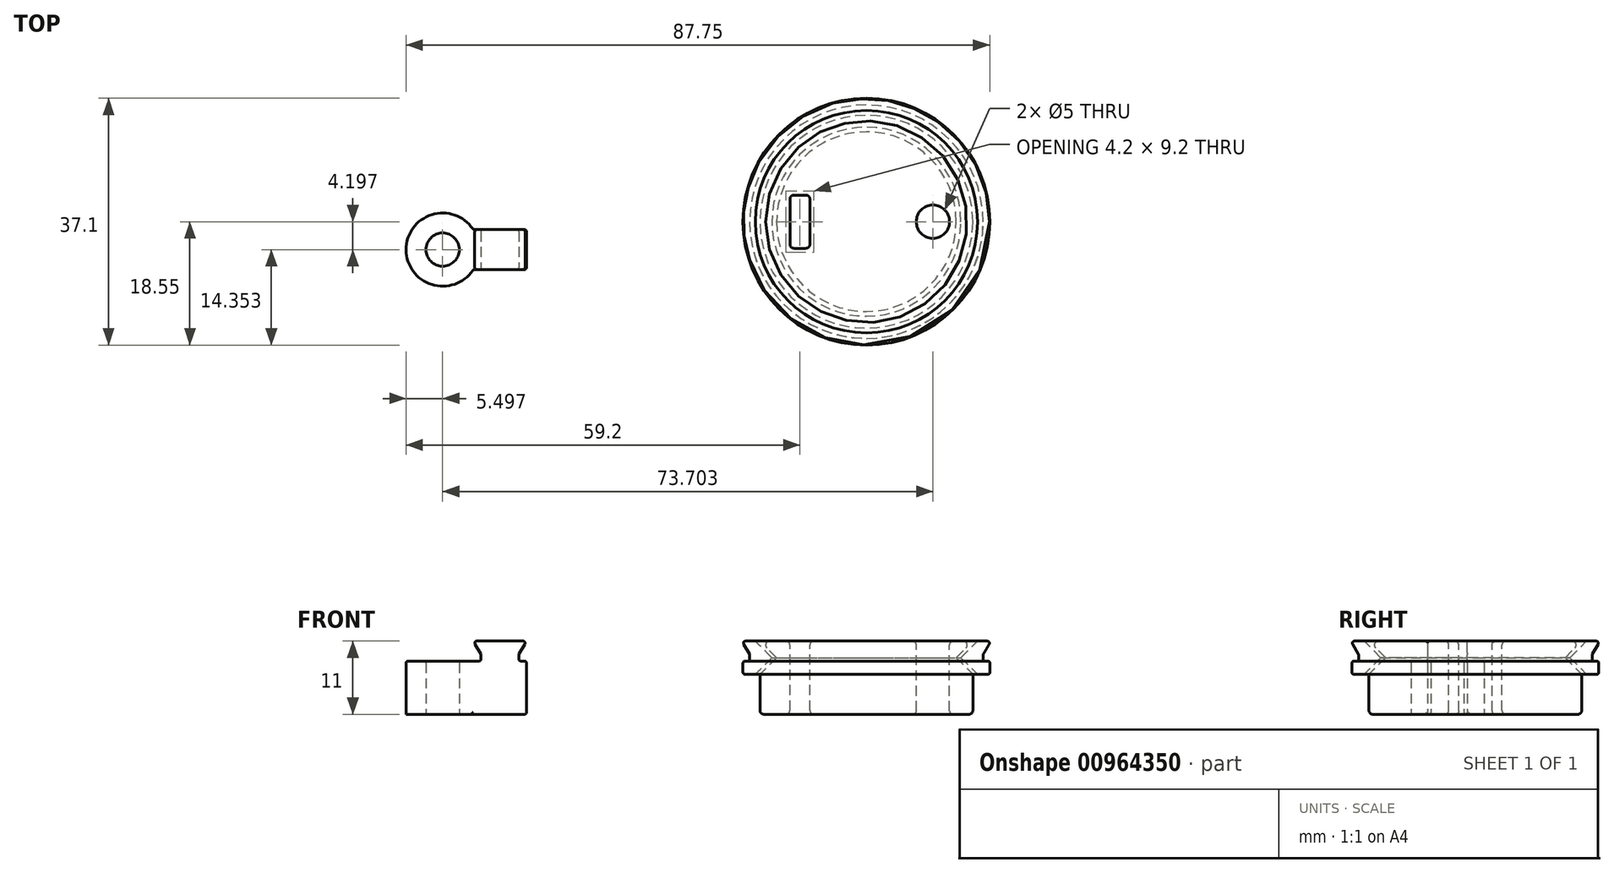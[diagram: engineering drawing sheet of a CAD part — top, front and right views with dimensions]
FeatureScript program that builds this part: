
annotation { "Feature Type Name" : "Feature", "Feature Type Description" : "" }
export const myFeature = defineFeature(function(context is Context, id is Id, definition is map)
    precondition{}
    {
        {
            assignVariable(context, id + "F0", {"variableType" : VariableType.LENGTH, "name" : "rise", "lengthValue" : 8 * mm});
        }
        {
            assignVariable(context, id + "F1", {"variableType" : VariableType.LENGTH, "name" : "upper", "lengthValue" : 3 * mm});
        }
        {
            var Q0;
            Q0=qCreatedBy(makeId("Front.planeOp"),FACE);
            var sketch = newSketch(context, id + "F2", { "sketchPlane" : qUnion([Q0])});
            skLineSegment(sketch, "E0.bottom", {"start": v(0, 0) * mm, "end": v(-16, 0) * mm});
            skLineSegment(sketch, "E0.top", {"start": v(0, 11) * mm, "end": v(-16, 11) * mm});
            skLineSegment(sketch, "E0.left", {"start": v(0, 0) * mm, "end": v(0, 11) * mm});
            skLineSegment(sketch, "E0.right", {"start": v(-16, 0) * mm, "end": v(-16, 6) * mm});
            skLineSegment(sketch, "E1", {"start": v(-16, 6) * mm, "end": v(-13.5, 8.5) * mm});
            skLineSegment(sketch, "E2", {"start": v(-13.5, 8.5) * mm, "end": v(-16, 11) * mm});
            skLineSegment(sketch, "E3.trimOffspring", {"start": v(-16, 11) * mm, "end": v(-16, 11) * mm});
            skLineSegment(sketch, "E4", {"start": v(-13.5, 8.5) * mm, "end": v(0, 8.5) * mm, "construction": true});
            skLineSegment(sketch, "E5", {"start": v(-14.2, 8.5) * mm, "end": v(-16.7, 6) * mm});
            skLineSegment(sketch, "E6", {"start": v(-16.7, 6) * mm, "end": v(-18.55, 6) * mm});
            skLineSegment(sketch, "E7", {"start": v(-18.7, 11) * mm, "end": v(-16.7, 11) * mm});
            skLineSegment(sketch, "E8", {"start": v(-16.7, 11) * mm, "end": v(-14.2, 8.5) * mm});
            skLineSegment(sketch, "E9", {"start": v(-18.55, 6) * mm, "end": v(-18.55, 8) * mm});
            skLineSegment(sketch, "E10", {"start": v(-18.55, 8) * mm, "end": v(-17.55, 8) * mm});
            skLineSegment(sketch, "E11", {"start": v(-17.55, 8) * mm, "end": v(-17.55, 9) * mm});
            skLineSegment(sketch, "E12", {"start": v(-17.55, 9) * mm, "end": v(-18.7, 11) * mm});
            skSolve(sketch);
        }
        {
            var Q0;
            Q0=makeQuery(id+"F2.imprint","IMPRINT",FACE,{"disambiguationData":[TD([[makeQuery(id+"F2.imprint","IMPRINT",EDGE,{"derivedFrom":sQuery(id+"F2.wireOp",EDGE,"E0.bottom")}),-1.0]])]});
            var Q1;
            Q1=makeQuery(id+"F2.imprint","IMPRINT",FACE,{"disambiguationData":[TD([[makeQuery(id+"F2.imprint","IMPRINT",EDGE,{"derivedFrom":sQuery(id+"F2.wireOp",EDGE,"hlnFj4VK-cs70-meuK-yrUh-ERZQpqiLJuiQ")}),-1.0]])]});
            var Q2;
            Q2=makeQuery(id+"F2.imprint","IMPRINT",FACE,{"disambiguationData":[TD([[makeQuery(id+"F2.imprint","IMPRINT",EDGE,{"derivedFrom":sQuery(id+"F2.wireOp",EDGE,"E5")}),-1.0]])]});
            var Q3;
            Q3=sQuery(id+"F2.wireOp",EDGE,"E0.left");
            revolve(context, id + "F3", {"surfaceOperationType" : NewSurfaceOperationType.NEW, "entities" : qUnion([Q0, Q1, Q2]), "axis" : qUnion([Q3]), "revolveType" : RevolveType.FULL});
        }
        {
            var Q0;
            Q0=makeQuery(id+"F3.opRevolve","SWEPT_FACE",FACE,{"disambiguationData":[OSD([sQuery(id+"F2.wireOp",EDGE,"E0.top")])]});
            var sketch = newSketch(context, id + "F4", { "sketchPlane" : qUnion([Q0])});
            skLineSegment(sketch, "E13", {"start": v(0, 0) * mm, "end": v(16, 0) * mm, "construction": true});
            skCircle(sketch, "E14", {"center": v(10, 0) * mm, "radius": 2.5 * mm});
            skCircle(sketch, "E15.cCircle", {"center": v(10, 0) * mm, "radius": 2.5 * mm, "construction": true});
            skLineSegment(sketch, "E16", {"start": v(0, 0) * mm, "end": v(-16, 0) * mm, "construction": true});
            skLineSegment(sketch, "E17.bottom", {"start": v(-8.5, -4) * mm, "end": v(-11.5, -4) * mm});
            skLineSegment(sketch, "E17.top", {"start": v(-8.5, 4) * mm, "end": v(-11.5, 4) * mm});
            skLineSegment(sketch, "E17.left", {"start": v(-8.5, -4) * mm, "end": v(-8.5, 4) * mm});
            skLineSegment(sketch, "E17.right", {"start": v(-11.5, -4) * mm, "end": v(-11.5, 4) * mm});
            skPoint(sketch, "E17.middle", {"position": v(-10, 0) * mm});
            skSolve(sketch);
        }
        {
            var Q0;
            Q0=makeQuery(id+"F4.imprint","IMPRINT",FACE,{"disambiguationData":[TD([[makeQuery(id+"F4.imprint","IMPRINT",EDGE,{"derivedFrom":sQuery(id+"F4.wireOp",EDGE,"E14")}),1.0]])]});
            extrude(context, id + "F5", {"entities" : qUnion([Q0]), "operationType" : NewBodyOperationType.REMOVE, "endBound" : BoundingType.THROUGH_ALL, "oppositeDirection" : true, "depth" : 25 * mm, "offsetDistance" : 25 * mm});
        }
        {
            var Q0;
            Q0 = qSketchRegion(id + "F4", true);
            extrude(context, id + "F6", {"entities" : qUnion([Q0]), "operationType" : NewBodyOperationType.REMOVE, "endBound" : BoundingType.THROUGH_ALL, "oppositeDirection" : true, "depth" : 4 * mm, "offsetDistance" : 25 * mm});
        }
        {
            var Q0;
            Q0=makeQuery(id+"F5.boolean.opBoolean","INTERSECT",EDGE,{"derivedFrom":[makeQuery(id+"F3.opRevolve","SWEPT_FACE",FACE,{"disambiguationData":[OSD([sQuery(id+"F2.wireOp",EDGE,"E0.bottom")])]}),makeQuery(id+"F5.opExtrude","SWEPT_FACE",FACE,{"disambiguationData":[OSD([sQuery(id+"F4.wireOp",EDGE,"E14")])]})]});
            var Q1;
            Q1=makeQuery(id+"F6.boolean.opBoolean","COPY",EDGE,{"derivedFrom":makeQuery(id+"F6.opExtrude","CAP_EDGE",EDGE,{"disambiguationData":[OSD([sQuery(id+"F4.wireOp",EDGE,"E15.0")])],"isStart":true})});
            var Q2;
            Q2=makeQuery(id+"F6.boolean.opBoolean","COPY",EDGE,{"derivedFrom":makeQuery(id+"F6.opExtrude","CAP_EDGE",EDGE,{"disambiguationData":[OSD([sQuery(id+"F4.wireOp",EDGE,"E15.5")])],"isStart":true})});
            var Q3;
            Q3=makeQuery(id+"F6.boolean.opBoolean","COPY",EDGE,{"derivedFrom":makeQuery(id+"F6.opExtrude","CAP_EDGE",EDGE,{"disambiguationData":[OSD([sQuery(id+"F4.wireOp",EDGE,"E15.4")])],"isStart":true})});
            var Q4;
            Q4=makeQuery(id+"F6.boolean.opBoolean","COPY",EDGE,{"derivedFrom":makeQuery(id+"F6.opExtrude","CAP_EDGE",EDGE,{"disambiguationData":[OSD([sQuery(id+"F4.wireOp",EDGE,"E15.3")])],"isStart":true})});
            var Q5;
            Q5=makeQuery(id+"F6.boolean.opBoolean","COPY",EDGE,{"derivedFrom":makeQuery(id+"F6.opExtrude","CAP_EDGE",EDGE,{"disambiguationData":[OSD([sQuery(id+"F4.wireOp",EDGE,"E15.2")])],"isStart":true})});
            var Q6;
            Q6=makeQuery(id+"F6.boolean.opBoolean","COPY",EDGE,{"derivedFrom":makeQuery(id+"F6.opExtrude","CAP_EDGE",EDGE,{"disambiguationData":[OSD([sQuery(id+"F4.wireOp",EDGE,"E15.1")])],"isStart":true})});
            fillet(context, id + "F7", {"entities" : qUnion([Q0, Q1, Q2, Q3, Q4, Q5, Q6]), "tangentPropagation" : true, "radius" : .5 * mm, "defaultsChanged" : false, "vertexSettings" : [], "allowEdgeOverflow" : false});
        }
        {
            var Q0;
            Q0=makeQuery(id+"F3.opRevolve","SWEPT_FACE",FACE,{"disambiguationData":[OSD([sQuery(id+"F2.wireOp",EDGE,"E0.top")])]});
            var Q1;
            Q1=makeQuery(id+"F3.opRevolve","SWEPT_FACE",FACE,{"disambiguationData":[OSD([sQuery(id+"F2.wireOp",EDGE,"E0.bottom")])]});
            var Q2;
            Q2=makeQuery(id+"F6.boolean.opBoolean","COPY",FACE,{"derivedFrom":makeQuery(id+"F6.opExtrude","SWEPT_FACE",FACE,{"disambiguationData":[OSD([sQuery(id+"F4.wireOp",EDGE,"E17.top")])]})});
            var Q3;
            Q3=makeQuery(id+"F6.boolean.opBoolean","COPY",FACE,{"derivedFrom":makeQuery(id+"F6.opExtrude","SWEPT_FACE",FACE,{"disambiguationData":[OSD([sQuery(id+"F4.wireOp",EDGE,"E17.bottom")])]})});
            fillet(context, id + "F8", {"entities" : qUnion([Q0, Q1, Q2, Q3]), "tangentPropagation" : true, "radius" : .6 * mm, "defaultsChanged" : false, "vertexSettings" : [], "allowEdgeOverflow" : false});
        }
        {
            var Q0;
            Q0=makeQuery(id+"F3.opRevolve","SWEPT_FACE",FACE,{"disambiguationData":[OSD([sQuery(id+"F2.wireOp",EDGE,"E11")])]});
            var Q1;
            Q1=makeQuery(id+"F3.opRevolve","SWEPT_FACE",FACE,{"disambiguationData":[OSD([sQuery(id+"F2.wireOp",EDGE,"E9")])]});
            var Q2;
            Q2=makeQuery(id+"F3.opRevolve","SWEPT_FACE",FACE,{"disambiguationData":[OSD([sQuery(id+"F2.wireOp",EDGE,"E12")])]});
            fillet(context, id + "F9", {"entities" : qUnion([Q0, Q1, Q2]), "tangentPropagation" : true, "radius" : .3 * mm, "defaultsChanged" : false, "vertexSettings" : [], "allowEdgeOverflow" : false});
        }
        {
            var Q0;
            Q0=qCreatedBy(makeId("Top.planeOp"),FACE);
            var sketch = newSketch(context, id + "F10", { "sketchPlane" : qUnion([Q0])});
            skCircle(sketch, "E18", {"center": v(-63.7, -4.2) * mm, "radius": 2.5 * mm});
            skCircle(sketch, "E19", {"center": v(-63.7, -4.2) * mm, "radius": 5.5 * mm});
            skLineSegment(sketch, "E20", {"start": v(-59.1, -1.2) * mm, "end": v(-51.1, -1.2) * mm});
            skLineSegment(sketch, "E21", {"start": v(-51.1, -1.2) * mm, "end": v(-51.1, -7.2) * mm});
            skLineSegment(sketch, "E22", {"start": v(-51.1, -7.2) * mm, "end": v(-59.1, -7.2) * mm});
            skLineSegment(sketch, "E23", {"start": v(-51.1, -4.2) * mm, "end": v(-63.7, -4.2) * mm, "construction": true});
            skSolve(sketch);
        }
        {
            var Q0;
            Q0=makeQuery(id+"F10.imprint","IMPRINT",FACE,{"disambiguationData":[TD([[makeQuery(id+"F10.imprint","IMPRINT",EDGE,{"derivedFrom":sQuery(id+"F10.wireOp",EDGE,"E18")}),-1.0]])]});
            var Q1;
            {var subQ0=sQuery(id+"F10.wireOp",EDGE,"E20");Q1=makeQuery(id+"F10.imprint","IMPRINT",FACE,{"disambiguationData":[TD([[makeQuery(id+"F10.imprint","IMPRINT",EDGE,{"derivedFrom":subQ0}),-1.0]])]});}
            extrude(context, id + "F11", {"entities" : qUnion([Q0, Q1]), "depth" : getVariable(context, 'rise'), "offsetDistance" : 25 * mm});
        }
        {
            var Q0;
            Q0=makeQuery(id+"F11.opExtrude","CAP_FACE",FACE,{"disambiguationData":[OSD([sQuery(id+"F10.wireOp",EDGE,"E18"),sQuery(id+"F10.wireOp",EDGE,"E19"),sQuery(id+"F10.wireOp",EDGE,"E20"),sQuery(id+"F10.wireOp",EDGE,"E21"),sQuery(id+"F10.wireOp",EDGE,"E22")])],"isStart":false});
            var sketch = newSketch(context, id + "F12", { "sketchPlane" : qUnion([Q0])});
            skArc(sketch, "E24.0.0", {"start": v(-59.1, -1.2) * mm, "mid": v(-69.2, -4.2) * mm, "end": v(-59.1, -7.2) * mm});
            skLineSegment(sketch, "E24.0.1", {"start": v(-59.1, -7.2) * mm, "end": v(-51.1, -7.2) * mm});
            skLineSegment(sketch, "E24.0.2", {"start": v(-51.1, -7.2) * mm, "end": v(-51.1, -1.2) * mm});
            skLineSegment(sketch, "E24.0.3", {"start": v(-51.1, -1.2) * mm, "end": v(-59.1, -1.2) * mm});
            skLineSegment(sketch, "E25", {"start": v(-59.1, -1.2) * mm, "end": v(-59.1, -7.2) * mm});
            skSolve(sketch);
        }
        {
            var Q0;
            Q0=makeQuery(id+"F12.imprint","IMPRINT",FACE,{"disambiguationData":[TD([[makeQuery(id+"F12.imprint","IMPRINT",EDGE,{"derivedFrom":sQuery(id+"F12.wireOp",EDGE,"E24.0.1")}),-1.0]])]});
            extrude(context, id + "F13", {"entities" : qUnion([Q0]), "operationType" : NewBodyOperationType.ADD, "depth" : getVariable(context, 'upper'), "offsetDistance" : 25 * mm});
        }
        {
            var Q0;
            Q0=makeQuery(id+"F13.boolean.opBoolean","MERGE",FACE,{"derivedFrom":[makeQuery(id+"F11.opExtrude","SWEPT_FACE",FACE,{"disambiguationData":[OSD([sQuery(id+"F10.wireOp",EDGE,"E22")])]}),makeQuery(id+"F13.opExtrude","SWEPT_FACE",FACE,{"disambiguationData":[OSD([sQuery(id+"F12.wireOp",EDGE,"E24.0.1")])]})]});
            var sketch = newSketch(context, id + "F14", { "sketchPlane" : qUnion([Q0])});
            skLineSegment(sketch, "E26", {"start": v(-59.1, 8) * mm, "end": v(-51.1, 8) * mm});
            skLineSegment(sketch, "E27", {"start": v(-59.1, 11) * mm, "end": v(-57.94, 9) * mm});
            skLineSegment(sketch, "E28", {"start": v(-57.94, 9) * mm, "end": v(-57.94, 8) * mm});
            skLineSegment(sketch, "E29", {"start": v(-51.1, 11) * mm, "end": v(-52.25, 9) * mm});
            skLineSegment(sketch, "E30", {"start": v(-52.25, 9) * mm, "end": v(-52.25, 8) * mm});
            skLineSegment(sketch, "E31", {"start": v(-57.94, 9) * mm, "end": v(-52.25, 9) * mm, "construction": true});
            skLineSegment(sketch, "E32", {"start": v(-55.1, 8) * mm, "end": v(-55.1, 11) * mm, "construction": true});
            skPoint(sketch, "E33", {"position": v(-55.1, 9) * mm});
            skSolve(sketch);
        }
        {
            var Q0;
            Q0=makeQuery(id+"F14.imprint","IMPRINT",FACE,{"disambiguationData":[TD([[makeQuery(id+"F14.imprint","IMPRINT",EDGE,{"derivedFrom":sQuery(id+"F14.wireOp",EDGE,"E27")}),-1.0]])]});
            var Q1;
            {var subQ5=sQuery(id+"F14.wireOp",EDGE,"E29");Q1=makeQuery(id+"F14.imprint","IMPRINT",FACE,{"disambiguationData":[TD([[makeQuery(id+"F14.imprint","IMPRINT",EDGE,{"derivedFrom":subQ5}),1.0]])]});}
            extrude(context, id + "F15", {"entities" : qUnion([Q0, Q1]), "operationType" : NewBodyOperationType.REMOVE, "endBound" : BoundingType.THROUGH_ALL, "oppositeDirection" : true, "depth" : 25 * mm, "offsetDistance" : 25 * mm});
        }
        {
            var Q0;
            Q0=makeQuery(id+"F13.opExtrude","CAP_FACE",FACE,{"disambiguationData":[OSD([sQuery(id+"F12.wireOp",EDGE,"E24.0.1"),sQuery(id+"F12.wireOp",EDGE,"E24.0.2"),sQuery(id+"F12.wireOp",EDGE,"E24.0.3"),sQuery(id+"F12.wireOp",EDGE,"E25")])],"isStart":false});
            var Q1;
            {var subQ0=sQuery(id+"F14.wireOp",EDGE,"E26");var subQ1=sQuery(id+"F10.wireOp",EDGE,"E22");var subQ2=sQuery(id+"F10.wireOp",EDGE,"E19");Q1=makeQuery(id+"F15.boolean.opBoolean","MERGE",FACE,{"derivedFrom":[makeQuery(id+"F11.opExtrude","CAP_FACE",FACE,{"disambiguationData":[OSD([sQuery(id+"F10.wireOp",EDGE,"E18"),subQ2,sQuery(id+"F10.wireOp",EDGE,"E20"),sQuery(id+"F10.wireOp",EDGE,"E21"),subQ1])],"isStart":false})],"fromTools":[makeQuery(id+"F15.opExtrude","SWEPT_FACE",FACE,{"disambiguationData":[OSD([subQ0]),TDD([makeQuery(id+"F14.imprint","IMPRINT",EDGE,{"disambiguationData":[TD([[makeQuery(id+"F14.imprint","INTERSECT",VERTEX,{"derivedFrom":[subQ0,sQuery(id+"F14.wireOp",EDGE,"E28")]}),1.0]])],"derivedFrom":subQ0})])]})]});}
            var Q2;
            Q2=makeQuery(id+"F15.boolean.opBoolean","COPY",FACE,{"derivedFrom":makeQuery(id+"F15.opExtrude","SWEPT_FACE",FACE,{"disambiguationData":[OSD([sQuery(id+"F14.wireOp",EDGE,"E28")])]})});
            var Q3;
            Q3=makeQuery(id+"F15.boolean.opBoolean","COPY",FACE,{"derivedFrom":makeQuery(id+"F15.opExtrude","SWEPT_FACE",FACE,{"disambiguationData":[OSD([sQuery(id+"F14.wireOp",EDGE,"E30")])]})});
            var Q4;
            Q4=makeQuery(id+"F13.boolean.opBoolean","MERGE",FACE,{"derivedFrom":[makeQuery(id+"F11.opExtrude","SWEPT_FACE",FACE,{"disambiguationData":[OSD([sQuery(id+"F10.wireOp",EDGE,"E22")])]}),makeQuery(id+"F13.opExtrude","SWEPT_FACE",FACE,{"disambiguationData":[OSD([sQuery(id+"F12.wireOp",EDGE,"E24.0.1")])]})]});
            var Q5;
            Q5=makeQuery(id+"F13.boolean.opBoolean","MERGE",FACE,{"derivedFrom":[makeQuery(id+"F11.opExtrude","SWEPT_FACE",FACE,{"disambiguationData":[OSD([sQuery(id+"F10.wireOp",EDGE,"E21")])]}),makeQuery(id+"F13.opExtrude","SWEPT_FACE",FACE,{"disambiguationData":[OSD([sQuery(id+"F12.wireOp",EDGE,"E24.0.2")])]})]});
            var Q6;
            Q6=makeQuery(id+"F11.opExtrude","CAP_EDGE",EDGE,{"disambiguationData":[OSD([sQuery(id+"F10.wireOp",EDGE,"E18")])],"isStart":true});
            var Q7;
            Q7=makeQuery(id+"F13.boolean.opBoolean","MERGE",FACE,{"derivedFrom":[makeQuery(id+"F11.opExtrude","SWEPT_FACE",FACE,{"disambiguationData":[OSD([sQuery(id+"F10.wireOp",EDGE,"E20")])]}),makeQuery(id+"F13.opExtrude","SWEPT_FACE",FACE,{"disambiguationData":[OSD([sQuery(id+"F12.wireOp",EDGE,"E24.0.3")])]})]});
            fillet(context, id + "F16", {"entities" : qUnion([Q0, Q1, Q2, Q3, Q4, Q5, Q6, Q7]), "tangentPropagation" : true, "radius" : .3 * mm, "defaultsChanged" : false, "vertexSettings" : [], "allowEdgeOverflow" : false});
        }
    });
